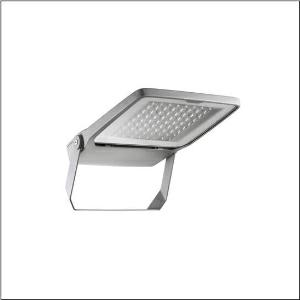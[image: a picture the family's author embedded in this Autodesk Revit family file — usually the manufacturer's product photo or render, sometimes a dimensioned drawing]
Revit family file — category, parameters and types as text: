
# Revit family: floodlight_fl_20_mini___pl43_5xa7672b1a1ac_c38e
name_source: partatom
category: Lighting Fixtures
units: mm (PartAtom-declared; Revit-internal decimal feet)

## family parameters
Cut with Voids When Loaded = No
Host = Face
Light Source = No
Part Type = Normal
Room Calculation Point = No
Round Connector Dimension = Use Diameter
Shared = No

## types (1)
- --- (1 x LED 3000K / CRI = 80 (unbekannt), 5220 lm, 3000K)
    Apparent Load = 51 VA
    CIE Flux Codes = 32 74 99 100 100
    Color Rendering = 80
    Color Temperature = 3000K
    Default Elevation = 1800 mm
    Description = Floodlight FL 20 mini, floodlight, primary light control with lens, of plastic, primary optical cover: protective disc, of toughened safety glass, transparent, light distribution: PL43, light emission: direct distribution, primary light characteristic: asymmetric, installation type: surface-mounted, LED, High Power LED, rated luminous flux: 5.220lm, luminous efficacy: 102lm/W, light colour: 830, colour temperature: 3000K, control gear: ECG Plus, control: flexible luminous flux parameterisation, time-dependent luminous flux control, digital communication interface, power reduction, overheat protection, electronic power reduction, with terminal, 5-pole, max. 2.5mm², mains connection: 220..240V, AC, 50/60Hz, rated input power: 51W, LED unit, of diecast aluminium, powder-coated, Siteco® metallic grey (DB 702S), corrosivity category C5 mid according to DIN EN ISO 12944, incl. 1x M20 cable gland for cable Ø 6.5..12mm, length: 446mm, width: 355mm, height: 62mm, housing frame, of diecast aluminium, powder-coated, Siteco® metallic grey (DB 702S), mounting bracket, of steel, powder-coated, Siteco® metallic grey (DB 702S), DALI, protection rating (complete): IP66, insulation class (complete): insulation class II (safety insulation), certification: CE, ENEC, VDE, protection symbol: D, permissible operating ambient temperature: -40..+40°C, permissible operating ambient temperature for outdoor applications: -40..+50°C, standard: DIN EN 12944, packaging unit: 1 piece

Light Distribution: PL43
    Height = 62 mm  [stored 0.203412 ft]
    Lamp = 1 x LED 3000K / CRI >= 80 (unbekannt)
    Lamp Light Flux = 5220 lm
    Lamp count = 1
    Length = 467 mm
    Luminous efficacy = 102 lm/W
    Manufacturer = Siteco
    ModVariant = No
    Model = 5XA7672B1A1AC
    Mounting Place = Wall
    Mounting Type = Surface mounted
    Number of Poles = 1
    OnlyDefault = Yes
    Power Factor = 1
    Product Name = Floodlight FL 20 mini | PL43
    Product group = floodlight | wall mounted
    ProductGroupID = 2001
    Protection Class = Protection class II
    Protection Degree = IP 66
    RLX_Detail_Level = 1
    RLX_Emergency_Light_Flux = 0 lm
    RLX_Emergency_Type = 0
    RLX_Emergency_Type_DB = No
    RlxData = <blob elided: 74021 chars, md5=cddf225c>
    Socket = socket
    Standby Power = 0 W
    System Light Flux = 5220 lm
    System Power = 51 W
    Type Comments = factory setting: luminous flux: 100 % | dim-lin: 254 | 520 mA
    Type Image = l_1005948.jpg
    URL = http://relux.com
    VarID = @adj_164429
    Voltage = 0 V
    Weight = 0.00 kg
    Width = 335 mm

note: [stored X ft] marks values corroborated as IEEE doubles in the binary element streams (Revit-internal decimal feet)

## geometry (parser evidence)
native form markers: Blend x4, Sweep x13
no freeform markers — native parametric forms only
